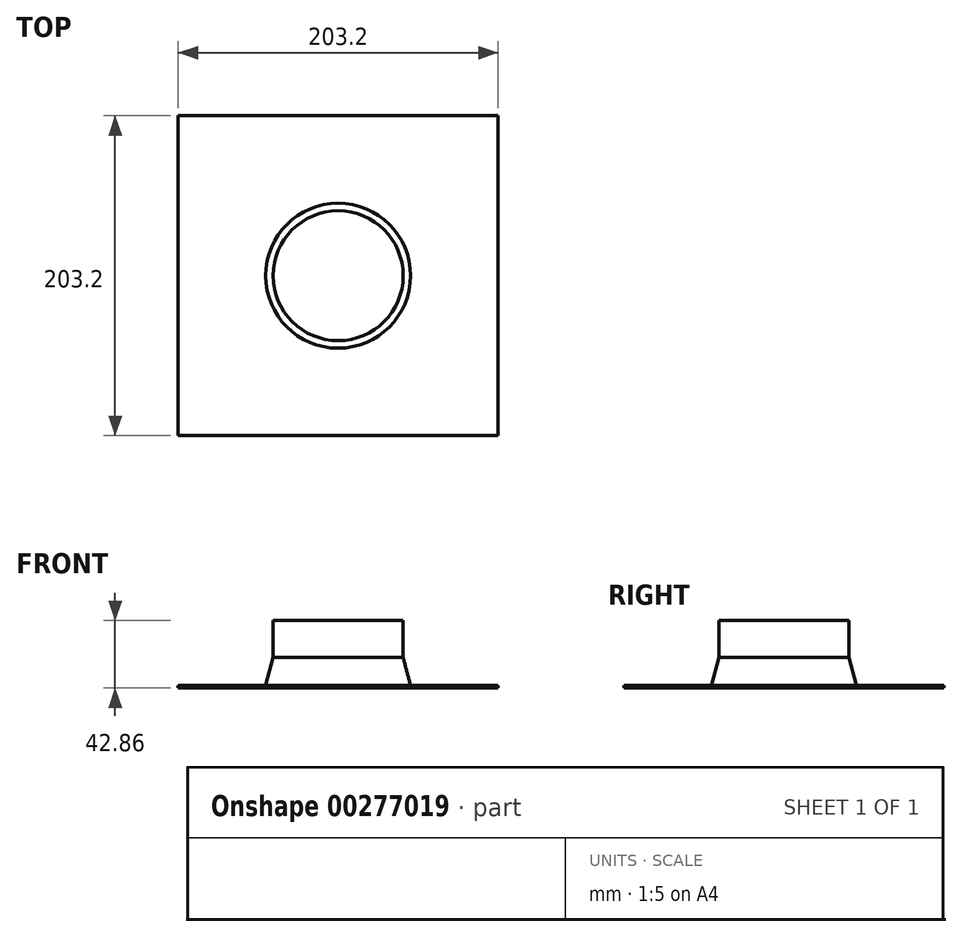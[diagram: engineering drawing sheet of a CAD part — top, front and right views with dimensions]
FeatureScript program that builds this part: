
annotation { "Feature Type Name" : "Feature", "Feature Type Description" : "" }
export const myFeature = defineFeature(function(context is Context, id is Id, definition is map)
    precondition{}
    {
        {
            var Q0;
            Q0=qCreatedBy(makeId("Top.planeOp"),FACE);
            var sketch = newSketch(context, id + "F0", { "sketchPlane" : qUnion([Q0])});
            skCircle(sketch, "E0", {"center": v(0, 0) * mm, "radius": 41.28 * mm});
            skSolve(sketch);
        }
        {
            var Q0;
            Q0=qCreatedBy(makeId("Top.planeOp"),FACE);
            cPlane(context, id + "F1", {"entities" : qUnion([Q0]), "cplaneType" : CPlaneType.OFFSET, "offset" : 41.27 * mm, "oppositeDirection" : true, "width" : 152.4 * mm, "height" : 152.4 * mm});
        }
        {
            var Q0;
            Q0=qCreatedBy(id+"F1.planeOp",FACE);
            var sketch = newSketch(context, id + "F2", { "sketchPlane" : qUnion([Q0])});
            skCircle(sketch, "E1", {"center": v(0, 0) * mm, "radius": 46.04 * mm});
            skSolve(sketch);
        }
        {
            var Q0;
            Q0 = qSketchRegion(id + "F2", true);
            extrude(context, id + "F3", {"entities" : qUnion([Q0]), "depth" : 19.05 * mm, "hasDraft" : true, "draftAngle" : 15 * degree, "draftPullDirection" : true});
        }
        {
            var Q0;
            Q0=makeQuery(id+"F0.imprint","IMPRINT",FACE,{"disambiguationData":[TD([[makeQuery(id+"F0.imprint","IMPRINT",EDGE,{"derivedFrom":sQuery(id+"F0.wireOp",EDGE,"E0")}),1.0]])]});
            extrude(context, id + "F4", {"entities" : qUnion([Q0]), "operationType" : NewBodyOperationType.ADD, "oppositeDirection" : true, "depth" : 25.4 * mm});
        }
        {
            var Q0;
            Q0=makeQuery(id+"F3.opExtrude","CAP_FACE",FACE,{"disambiguationData":[OSD([sQuery(id+"F2.wireOp",EDGE,"E1")])],"isStart":true});
            var sketch = newSketch(context, id + "F5", { "sketchPlane" : qUnion([Q0])});
            skLineSegment(sketch, "E2", {"start": v(0, 0) * mm, "end": v(101.6, 0) * mm});
            skLineSegment(sketch, "E3", {"start": v(101.6, 0) * mm, "end": v(101.6, 101.6) * mm});
            skLineSegment(sketch, "E4", {"start": v(101.6, 101.6) * mm, "end": v(-101.6, 101.6) * mm});
            skLineSegment(sketch, "E5", {"start": v(-101.6, 101.6) * mm, "end": v(-101.6, -101.6) * mm});
            skLineSegment(sketch, "E6", {"start": v(-101.6, -101.6) * mm, "end": v(101.6, -101.6) * mm});
            skLineSegment(sketch, "E7", {"start": v(101.6, -101.6) * mm, "end": v(101.6, 0) * mm});
            skSolve(sketch);
        }
        {
            var Q0;
            Q0=makeQuery(id+"F5.imprint","IMPRINT",FACE,{"disambiguationData":[TD([[makeQuery(id+"F5.imprint","IMPRINT",EDGE,{"derivedFrom":sQuery(id+"F5.wireOp",EDGE,"E3")}),1.0]])]});
            var Q1;
            Q1=makeQuery(id+"F5.imprint","IMPRINT",FACE,{"disambiguationData":[TD([[makeQuery(id+"F5.imprint","IMPRINT",EDGE,{"derivedFrom":makeQuery(id+"F3.opExtrude","CAP_EDGE",EDGE,{"disambiguationData":[OSD([sQuery(id+"F2.wireOp",EDGE,"E1")])],"isStart":true})}),-1.0]])]});
            extrude(context, id + "F6", {"entities" : qUnion([Q0, Q1]), "depth" : 1.59 * mm, "offsetDistance" : 25.4 * mm});
        }
    });
